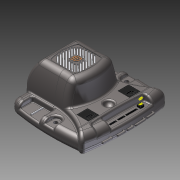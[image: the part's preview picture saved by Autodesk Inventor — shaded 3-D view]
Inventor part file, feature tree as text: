
AUTODESK INVENTOR PART (.ipt)
format: ipt  version: 2011 (Build 150239000, 239)  size: 3,033,600 bytes
history: native  units: mm
features: other x11, sketch x9, extrude x9, plane x5, mirror x3, imported_body x1, emboss x1
ambient origin geometry x8: Origin, YZ Plane, XZ Plane, XY Plane, X Axis, Y Axis, Z Axis, Center Point
bodies: Solid1 (feature_tree)
feature tree (39):
  imported_body  "Base1"
  emboss  "Emboss1"
  sketch  "Sketch1"  dims[d50=0.9144mm d57=1.467403mm]
  extrude  "Extrusion2"  Depth=1.467403mm
  plane  "Work Plane1"
  mirror  "Mirror1"
  extrude  "Extrusion3"  Depth=1.467403mm
  sketch  "Sketch2"  dims[d58=1.467403mm d59=1.467403mm]
  extrude  "Extrusion4"  Depth=1.467403mm
  extrude  "Extrusion6"  Depth=1.467403mm
  extrude  "Extrusion7"  TaperAngle=90.0deg  [1 undecoded]
  mirror  "Mirror2"
  extrude  "Extrusion8"  Depth=9.7282mm
  mirror  "Mirror3"
  sketch  "Sketch5"  dims[d62=1.467403mm d63=1.467403mm]
  other  "Work Axis1"
  extrude  "Extrusion9"  Depth=0.762mm
  plane  "Work Plane2"
  extrude  "Extrusion10"  Depth=0.254mm TaperAngle=0.0deg
  extrude  "Extrusion12"  Depth=1.27mm
  sketch  "Sketch12"  dims[d80=2.54mm d81=0.0mm d82=0.254mm d83=0.0mm]
  other  "Work Point1"
  other  "Work Point2"
  other  "Work Point3"
  other  "Work Point7"
  other  "Work Point8"
  other  "Work Point9"
  sketch  "Sketch4"  dims[d60=1.467403mm d61=1.467403mm]
  sketch  "Sketch6"  dims[d66=1.27mm d67=0.0mm d70=90.0deg]
  sketch  "Sketch7"  dims[d71=1.27mm d72=0.0mm d73=9.7282mm]
  other  "Image2"
  sketch  "Sketch11"  dims[d75=0.762mm d76=0.0mm d77=0.762mm]
  plane  "Work Plane3"
  other  "Work Axis2"
  plane  "Work Plane4"
  other  "Work Axis3"
  plane  "Work Plane5"
  other  "Work Axis4"
  sketch  "Sketch14"  dims[d84=1.016mm d85=0.0mm d86=1.27mm d87=2.286mm d88=4.572mm d89=4.572mm d90=3.81mm d91=0.0mm d92=-15.24mm d105=129.575698mm d160=0.254mm d162=1.27mm d169=0.635mm d182=1.27mm d183=0.0mm d187=6.35mm d188=0.0mm d191=6.35mm d192=6.35mm d193=6.35mm d238=7.9375mm d239=7.9375mm d244=3.96875mm d245=1.133929mm d248=0.762mm d249=0.0mm]
note: 1 required parameter value undecoded (feature->parameter linkage not recoverable at this tier; creation-order binding heuristic only, values carry confidence <= 0.55)
